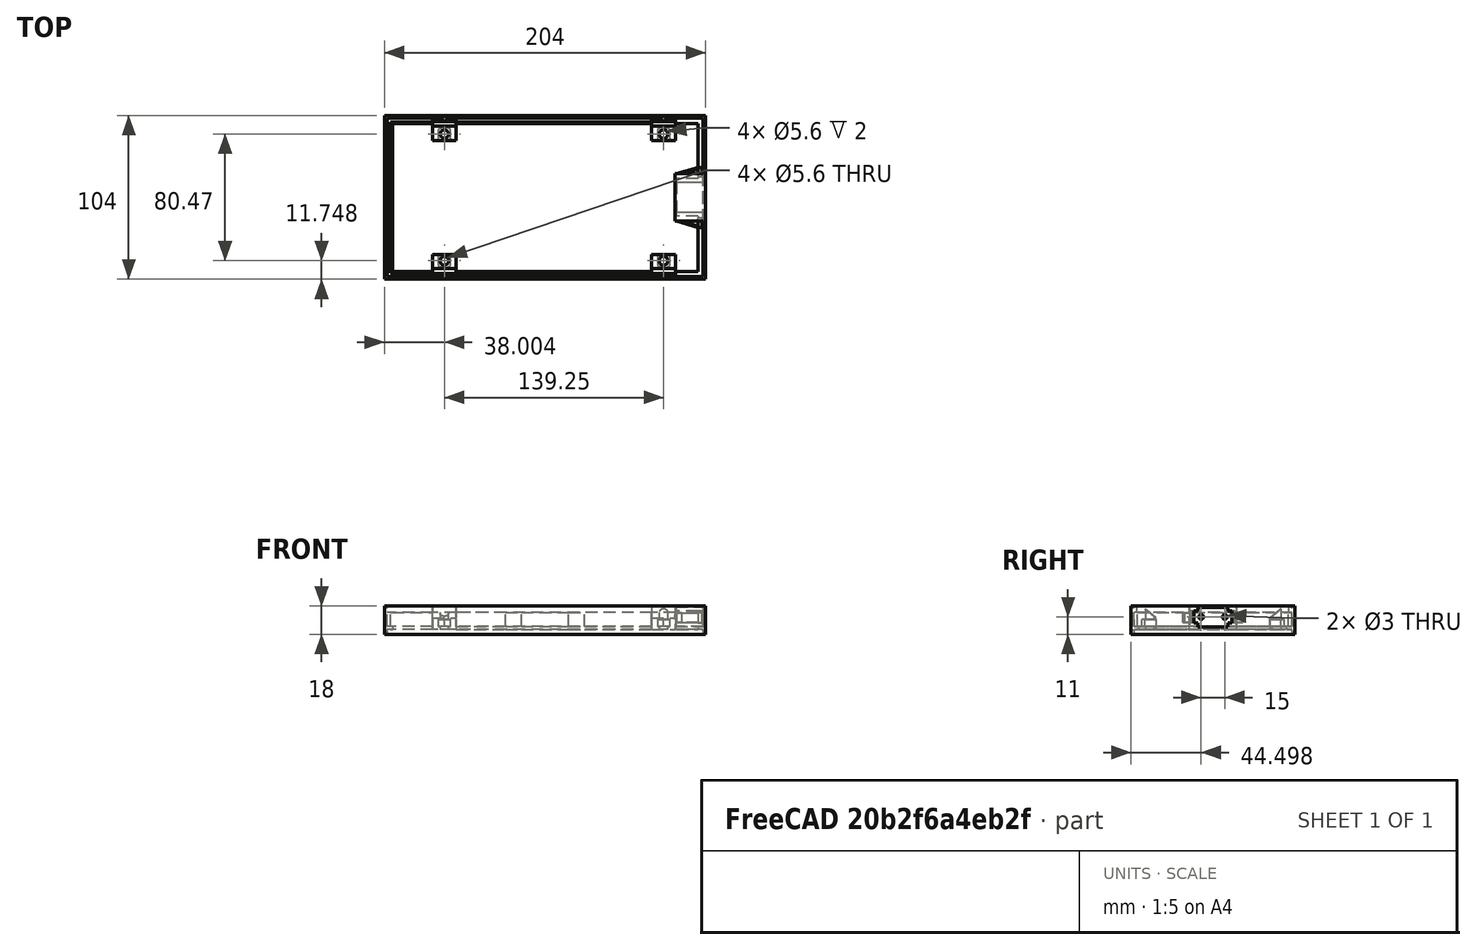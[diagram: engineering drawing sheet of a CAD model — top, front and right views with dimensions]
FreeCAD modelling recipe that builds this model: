
FCSTD DOCUMENT  (FreeCAD 0.18.3R)
Label: lamp.base.frame.230V.flat.shortside
License: All rights reserved
LicenseURL: http://en.wikipedia.org/wiki/All_rights_reserved
objects: Part::Extrusion×93, Part::Part2DObjectPython×50, Part::Cut×48, Part::Feature×38, Part::MultiFuse×21
note: 250 computed .brp shape members not serialized (recipe doc carries the construction recipe); baked Part::Feature solids carry a one-line shape summary decoded from their .brp

FEATURE [Part::Feature] Face035
  Placement = pos=(286.998,-351.852,-5.08221) rot=(0.57735,0.57735,0.57735;2.0944rad)
  shape: bbox 2e-07 x 3 x 7.5 mm, 1 faces, 0 solids (baked)
FEATURE [Part::Extrusion] Extrusion040
  Base = -> Face035
  Dir = (11.952,0,0)
  DirMode = 0
  FaceMakerClass = Part::FaceMakerBullseye
  LengthFwd = 0
  LengthRev = 0
  Solid = true
  Symmetric = false
FEATURE [Part::Part2DObjectPython] Rectangle114  # Draft 2D object (typed FeaturePython)
  ChamferSize = 0
  Columns = 1
  FilletRadius = 0
  Height = 14
  Length = 15
  MakeFace = true
  Placement = pos=(-44.4799,-326.495,6.4) rot=(0,0,1;0rad)
  Rows = 1
FEATURE [Part::Feature] Face048
  shape: bbox 4e-07 x 5 x 18 mm, 1 faces, 0 solids (baked)
FEATURE [Part::Part2DObjectPython] Circle027  # Draft 2D object (typed FeaturePython)
  FirstAngle = 0
  LastAngle = 0
  MakeFace = true
  Placement = pos=(-36.9799,-236.025,2.5e-14) rot=(1,0,0;3.14159rad)
  Radius = 2.8
FEATURE [Part::Part2DObjectPython] Rectangle106  # Draft 2D object (typed FeaturePython)
  ChamferSize = 0
  Columns = 1
  FilletRadius = 0
  Height = 14.0305
  Length = 15
  MakeFace = true
  Placement = pos=(-44.4799,-240.025,6) rot=(0,0,1;0rad)
  Rows = 1
FEATURE [Part::Part2DObjectPython] Circle058  # Draft 2D object (typed FeaturePython)
  FirstAngle = 0
  LastAngle = 0
  MakeFace = true
  Placement = pos=(141.399,-335.352,2) rot=(1,0,0;1.5708rad)
  Radius = 1.5
FEATURE [Part::Feature] Face037
  Placement = pos=(258.998,-351.852,-5.08221) rot=(0.57735,0.57735,0.57735;2.0944rad)
  shape: bbox 2e-07 x 3 x 7.5 mm, 1 faces, 0 solids (baked)
FEATURE [Part::Part2DObjectPython] Circle024  # Draft 2D object (typed FeaturePython)
  FirstAngle = 0
  LastAngle = 0
  MakeFace = true
  Placement = pos=(-176.23,-316.495,1.32e-13) rot=(1,0,0;3.14159rad)
  Radius = 2.8
FEATURE [Part::Part2DObjectPython] Wire005  # Draft 2D object (typed FeaturePython)
  ChamferSize = 0
  Closed = true
  End = (-172.23,-313.495,6)
  FilletRadius = 0
  Length = 29.8885
  MakeFace = true
  Placement = pos=(-176.23,-311.495,6) rot=(0,0,1;0rad)
  Points = (6) [(0,0,0),(-4,-2,-1.77636e-15),(-4,-8,0),(0,-10,0),(4,-8,8.88178e-16),(4,-2,1.77636e-15)]
  Start = (-176.23,-311.495,6)
  Subdivisions = 0
FEATURE [Part::Extrusion] Extrude150
  Base = -> Wire005
  Dir = (0,0,1)
  DirMode = 2
  FaceMakerClass = Part::FaceMakerBullseye
  LengthFwd = 4.4
  LengthRev = 0
  Placement = pos=(-2.8e-14,0,-4) rot=(0,0,1;0rad)
  Solid = false
  Symmetric = false
FEATURE [Part::Extrusion] Extrude151
  Base = -> Wire005
  Dir = (0,0,1)
  DirMode = 2
  FaceMakerClass = Part::FaceMakerBullseye
  LengthFwd = 4.4
  LengthRev = 0
  Placement = pos=(-2.8e-14,80.4695,-4) rot=(0,0,1;0rad)
  Solid = false
  Symmetric = false
FEATURE [Part::Extrusion] Extrude152
  Base = -> Wire005
  Dir = (0,0,1)
  DirMode = 2
  FaceMakerClass = Part::FaceMakerBullseye
  LengthFwd = 4.4
  LengthRev = 0
  Placement = pos=(139.25,0,-4) rot=(0,0,1;0rad)
  Solid = false
  Symmetric = false
FEATURE [Part::Extrusion] Extrude230
  Base = -> Circle058
  Dir = (0,-1,-2e-16)
  DirMode = 2
  FaceMakerClass = Part::FaceMakerBullseye
  LengthFwd = -2
  LengthRev = 0
  Solid = false
  Symmetric = false
FEATURE [Part::Extrusion] Extrude156
  Base = -> Rectangle106
  Dir = (0,0,1)
  DirMode = 2
  FaceMakerClass = Part::FaceMakerBullseye
  LengthFwd = -6.4
  LengthRev = 0
  Placement = pos=(0,0,0.4) rot=(0,0,1;0rad)
  Solid = false
  Symmetric = false
FEATURE [Part::Part2DObjectPython] Rectangle164  # Draft 2D object (typed FeaturePython)
  ChamferSize = 0
  Columns = 1
  FilletRadius = 0
  Height = 7
  Length = 2.5
  MakeFace = true
  Placement = pos=(131.899,-351.602,-1.5) rot=(0.57735,0.57735,0.57735;2.0944rad)
  Rows = 1
FEATURE [Part::Part2DObjectPython] Circle040  # Draft 2D object (typed FeaturePython)
  FirstAngle = 0
  LastAngle = 0
  MakeFace = true
  Placement = pos=(218.524,-261.633,-6) rot=(1,0,0;3.14159rad)
  Radius = 2.8
FEATURE [Part::Part2DObjectPython] Rectangle  # Draft 2D object (typed FeaturePython)
  ChamferSize = 0
  Columns = 1
  FilletRadius = 0
  Height = 14
  Length = 15
  MakeFace = true
  Placement = pos=(-183.73,-326.495,6) rot=(0,0,1;0rad)
  Rows = 1
FEATURE [Part::Extrusion] Extrude158
  Base = -> Rectangle
  Dir = (0,0,1)
  DirMode = 2
  FaceMakerClass = Part::FaceMakerBullseye
  LengthFwd = -6.4
  LengthRev = 0
  Placement = pos=(0,0,0.4) rot=(0,0,1;0rad)
  Solid = false
  Symmetric = false
FEATURE [Part::Part2DObjectPython] Rectangle162  # Draft 2D object (typed FeaturePython)
  ChamferSize = 0
  Columns = 1
  FilletRadius = 0
  Height = 0.2
  Length = 19
  MakeFace = true
  Placement = pos=(139.399,-353.852,-4.2) rot=(1,0,0;1.5708rad)
  Rows = 1
FEATURE [Part::Extrusion] Extrude231
  Base = -> Rectangle162
  Dir = (-3e-16,-1,2e-16)
  DirMode = 2
  FaceMakerClass = Part::FaceMakerBullseye
  LengthFwd = 10
  LengthRev = 0
  Placement = pos=(0,5,-9e-16) rot=(0,0,1;0rad)
  Solid = false
  Symmetric = false
FEATURE [Part::Feature] Face047
  Placement = pos=(-124.099,0,3.33221) rot=(0,0,1;0rad)
  shape: bbox 2 x 3e-07 x 7.5 mm, 1 faces, 0 solids (baked)
FEATURE [Part::Extrusion] Extrusion039
  Base = -> Rectangle
  Dir = (-28,0,0)
  DirMode = 0
  FaceMakerClass = Part::FaceMakerBullseye
  LengthFwd = 0
  LengthRev = 0
  Solid = true
  Symmetric = false
FEATURE [Part::Feature] Face038
  Placement = pos=(134.899,-349.102,5.25) rot=(0,0,1;3.14159rad)
  shape: bbox 5.5 x 2.5 x 2e-07 mm, 1 faces, 0 solids (baked)
FEATURE [Part::Extrusion] Extrusion044
  Base = -> Face038
  Dir = (0,1e-16,0.5)
  DirMode = 0
  FaceMakerClass = Part::FaceMakerBullseye
  LengthFwd = 0
  LengthRev = 0
  Solid = true
  Symmetric = false
FEATURE [Part::Feature] Face044
  Placement = pos=(-124.099,0,3.33221) rot=(0,0,1;0rad)
  shape: bbox 19 x 18.5 x 2e-07 mm, 1 faces, 0 solids (baked)
FEATURE [Part::Extrusion] Extrusion052
  Base = -> Face044
  Dir = (0,0,-0.2)
  DirMode = 0
  FaceMakerClass = Part::FaceMakerBullseye
  LengthFwd = 0
  LengthRev = 0
  Solid = true
  Symmetric = false
FEATURE [Part::Extrusion] Extrude155
  Base = -> Circle027
  Dir = (0,0,-1)
  DirMode = 2
  FaceMakerClass = Part::FaceMakerBullseye
  LengthFwd = -6.4
  LengthRev = 0
  Solid = false
  Symmetric = false
FEATURE [Part::Part2DObjectPython] Rectangle159  # Draft 2D object (typed FeaturePython)
  ChamferSize = 0
  Columns = 1
  FilletRadius = 0
  Height = 14.3
  Length = 1
  MakeFace = true
  Placement = pos=(166.939,-349.382,5.5) rot=(0,0,1;0.283123rad)
  Rows = 1
FEATURE [Part::Extrusion] Extrusion042
  Base = -> Face037
  Dir = (-14.0793,0,0)
  DirMode = 0
  FaceMakerClass = Part::FaceMakerBullseye
  LengthFwd = 0
  LengthRev = 0
  Solid = true
  Symmetric = false
FEATURE [Part::Extrusion] Extrusion059
  Base = -> Face048
  Dir = (50,1.5e-15,0)
  DirMode = 0
  FaceMakerClass = Part::FaceMakerBullseye
  LengthFwd = 0
  LengthRev = 0
  Solid = true
  Symmetric = false
FEATURE [Part::Part2DObjectPython] Rectangle073  # Draft 2D object (typed FeaturePython)
  ChamferSize = 0
  Columns = 1
  FilletRadius = 0
  Height = 100.5
  Length = 200.5
  MakeFace = true
  Placement = pos=(-212.48,-326.495,-1) rot=(0,0,1;0rad)
  Rows = 1
FEATURE [Part::Feature] Face050
  Placement = pos=(39.6248,-78.9998,4e-15) rot=(0,0,1;0rad)
  shape: bbox 1 x 3e-07 x 7.5 mm, 1 faces, 0 solids (baked)
FEATURE [Part::Feature] Face039
  Placement = pos=(0,0,-0.25) rot=(0,0,1;0rad)
  shape: bbox 2e-07 x 2.5 x 0.5 mm, 1 faces, 0 solids (baked)
FEATURE [Part::Extrusion] Extrusion045
  Base = -> Face039
  Dir = (2.49999,0,0)
  DirMode = 0
  FaceMakerClass = Part::FaceMakerBullseye
  LengthFwd = 0
  LengthRev = 0
  Solid = true
  Symmetric = false
FEATURE [Part::Part2DObjectPython] Rectangle111  # Draft 2D object (typed FeaturePython)
  ChamferSize = 0
  Columns = 1
  FilletRadius = 0
  Height = 4.4
  Length = 8
  MakeFace = true
  Placement = pos=(-32.9799,-313.495,2) rot=(0,0.707107,0.707107;3.14159rad)
  Rows = 1
FEATURE [Part::Extrusion] Extrude160
  Base = -> Rectangle111
  Dir = (0,1,-2e-16)
  DirMode = 2
  FaceMakerClass = Part::FaceMakerBullseye
  LengthFwd = 8
  LengthRev = 0
  Solid = false
  Symmetric = false
FEATURE [Part::Extrusion] Extrude237
  Base = -> Rectangle164
  Dir = (1,0,0)
  DirMode = 2
  FaceMakerClass = Part::FaceMakerBullseye
  LengthFwd = -2
  LengthRev = 0
  Solid = false
  Symmetric = false
FEATURE [Part::Part2DObjectPython] Rectangle113  # Draft 2D object (typed FeaturePython)
  ChamferSize = 0
  Columns = 1
  FilletRadius = 0
  Height = 14.0305
  Length = 15
  MakeFace = true
  Placement = pos=(-183.73,-240.025,6.4) rot=(0,0,1;0rad)
  Rows = 1
FEATURE [Part::Extrusion] Extrude
  Base = -> Circle024
  Dir = (0,0,-1)
  DirMode = 2
  FaceMakerClass = Part::FaceMakerBullseye
  LengthFwd = -6.4
  LengthRev = 0
  Solid = false
  Symmetric = false
FEATURE [Part::Part2DObjectPython] Rectangle074  # Draft 2D object (typed FeaturePython)
  ChamferSize = 0
  Columns = 1
  FilletRadius = 0
  Height = 96
  Length = 196
  MakeFace = true
  Placement = pos=(-210.23,-324.245,4.41e-14) rot=(0,0,1;0rad)
  Rows = 1
FEATURE [Part::Part2DObjectPython] Circle057  # Draft 2D object (typed FeaturePython)
  FirstAngle = 0
  LastAngle = 0
  MakeFace = true
  Placement = pos=(156.399,-335.352,2) rot=(1,0,0;1.5708rad)
  Radius = 1.5
FEATURE [Part::Extrusion] Extrude229
  Base = -> Circle057
  Dir = (0,-1,-2e-16)
  DirMode = 2
  FaceMakerClass = Part::FaceMakerBullseye
  LengthFwd = -2
  LengthRev = 0
  Solid = false
  Symmetric = false
FEATURE [Part::Extrusion] Extrude100
  Base = -> Rectangle073
  Dir = (0,2e-16,1)
  DirMode = 2
  FaceMakerClass = Part::FaceMakerBullseye
  LengthFwd = 2
  LengthRev = 0
  Placement = pos=(0,0,1) rot=(0,0,1;0rad)
  Solid = false
  Symmetric = false
FEATURE [Part::Part2DObjectPython] Rectangle109  # Draft 2D object (typed FeaturePython)
  ChamferSize = 0
  Columns = 1
  FilletRadius = 0
  Height = 4.4
  Length = 8
  MakeFace = true
  Placement = pos=(-172.23,-239.025,2) rot=(0,0.707107,0.707107;3.14159rad)
  Rows = 1
FEATURE [Part::Extrusion] Extrude162
  Base = -> Rectangle109
  Dir = (0,1,-2e-16)
  DirMode = 2
  FaceMakerClass = Part::FaceMakerBullseye
  LengthFwd = -8
  LengthRev = 0
  Solid = false
  Symmetric = false
FEATURE [Part::Extrusion] Extrude101
  Base = -> Rectangle074
  Dir = (0,2e-16,1)
  DirMode = 2
  FaceMakerClass = Part::FaceMakerBullseye
  LengthFwd = 10
  LengthRev = 0
  Solid = false
  Symmetric = false
FEATURE [Part::Part2DObjectPython] Rectangle107  # Draft 2D object (typed FeaturePython)
  ChamferSize = 0
  Columns = 1
  FilletRadius = 0
  Height = 14.0305
  Length = 15
  MakeFace = true
  Placement = pos=(-183.73,-240.025,6) rot=(0,0,1;0rad)
  Rows = 1
FEATURE [Part::Extrusion] Extrude157
  Base = -> Rectangle107
  Dir = (0,0,1)
  DirMode = 2
  FaceMakerClass = Part::FaceMakerBullseye
  LengthFwd = -6.4
  LengthRev = 0
  Placement = pos=(0,0,0.4) rot=(0,0,1;0rad)
  Solid = false
  Symmetric = false
FEATURE [Part::Cut] Cut054
  Base = -> Extrude157
  Tool = -> Extrude151
FEATURE [Part::Part2DObjectPython] Wire  # Draft 2D object (typed FeaturePython)
  ChamferSize = 0
  Closed = true
  End = (260.998,-353.852,-5.08221)
  FilletRadius = 0
  Length = 72
  MakeFace = true
  Placement = pos=(260.998,-353.852,2.41779) rot=(1,0,0;1.5708rad)
  Points = (12) [(0,0,0),(2.5,1.33227e-15,0),(2.5,2.25,0),(21.5,2.25,0),(21.5,8.88178e-16,0),(24,4.44089e-16,0),(24,-7.5,0),(21.5,-7.5,0),(21.5,-9.75,0),(2.5,-9.75,0),(2.5,-7.5,0),(0,-7.5,0)]
  Start = (260.998,-353.852,2.41779)
  Subdivisions = 0
FEATURE [Part::Part2DObjectPython] Rectangle110  # Draft 2D object (typed FeaturePython)
  ChamferSize = 0
  Columns = 1
  FilletRadius = 0
  Height = 4.4
  Length = 8
  MakeFace = true
  Placement = pos=(-172.23,-313.495,2) rot=(0,0.707107,0.707107;3.14159rad)
  Rows = 1
FEATURE [Part::Extrusion] Extrude161
  Base = -> Rectangle110
  Dir = (0,1,-2e-16)
  DirMode = 2
  FaceMakerClass = Part::FaceMakerBullseye
  LengthFwd = 8
  LengthRev = 0
  Solid = false
  Symmetric = false
FEATURE [Part::Part2DObjectPython] Rectangle071  # Draft 2D object (typed FeaturePython)
  ChamferSize = 0
  Columns = 1
  FilletRadius = 0
  Height = 100.5
  Length = 200.5
  MakeFace = true
  Placement = pos=(-212.48,-326.495,-1) rot=(0,0,1;0rad)
  Rows = 1
FEATURE [Part::Part2DObjectPython] Rectangle072  # Draft 2D object (typed FeaturePython)
  ChamferSize = 0
  Columns = 1
  FilletRadius = 0
  Height = 104
  Length = 204
  MakeFace = true
  Placement = pos=(-214.23,-328.245,-1) rot=(0,0,1;0rad)
  Rows = 1
  Support = -> [Rectangle071]
FEATURE [Part::Extrusion] Extrude099
  Base = -> Rectangle072
  Dir = (0,2e-16,1)
  DirMode = 2
  FaceMakerClass = Part::FaceMakerBullseye
  LengthFwd = 16
  LengthRev = 0
  Solid = false
  Symmetric = false
FEATURE [Part::Extrusion] Extrude098
  Base = -> Rectangle071
  Dir = (0,2e-16,1)
  DirMode = 2
  FaceMakerClass = Part::FaceMakerBullseye
  LengthFwd = 16
  LengthRev = 0
  Solid = false
  Symmetric = false
FEATURE [Part::Part2DObjectPython] Rectangle160  # Draft 2D object (typed FeaturePython)
  ChamferSize = 0
  Columns = 1
  FilletRadius = 0
  Height = 14.3
  Length = 0.88
  MakeFace = true
  Placement = pos=(129.899,-349.102,5.5) rot=(0,0,-1;0.283566rad)
  Rows = 1
FEATURE [Part::Part2DObjectPython] Rectangle117  # Draft 2D object (typed FeaturePython)
  ChamferSize = 0
  Columns = 1
  FilletRadius = 0
  Height = 2
  Length = 200.5
  MakeFace = true
  Placement = pos=(-212.48,-227.995,15) rot=(0,0,1;0rad)
  Rows = 1
FEATURE [Part::Part2DObjectPython] Wire008  # Draft 2D object (typed FeaturePython)
  ChamferSize = 0
  Closed = true
  End = (-183.73,-312.495,7.4)
  FilletRadius = 0
  Length = 28.3796
  MakeFace = true
  Placement = pos=(-183.73,-321.495,15) rot=(0,0,1;0rad)
  Points = (3) [(0,0,0),(0,9,0),(0,9,-7.6)]
  Start = (-183.73,-321.495,15)
  Subdivisions = 0
FEATURE [Part::Part2DObjectPython] Rectangle116  # Draft 2D object (typed FeaturePython)
  ChamferSize = 0
  Columns = 1
  FilletRadius = 0
  Height = 2
  Length = 200.5
  MakeFace = true
  Placement = pos=(-212.48,-326.495,15) rot=(0,0,1;0rad)
  Rows = 1
FEATURE [Part::Part2DObjectPython] Wire009  # Draft 2D object (typed FeaturePython)
  ChamferSize = 0
  Closed = true
  End = (-29.4799,-312.495,7.4)
  FilletRadius = 0
  Length = 28.3796
  MakeFace = true
  Placement = pos=(-29.4799,-321.495,15) rot=(0,0,1;0rad)
  Points = (3) [(0,0,0),(0,9,1.77636e-15),(0,9,-7.6)]
  Start = (-29.4799,-321.495,15)
  Subdivisions = 0
FEATURE [Part::Feature] Face040
  Placement = pos=(0,0,-0.25) rot=(0,0,1;0rad)
  shape: bbox 2e-07 x 2.5 x 6.5 mm, 1 faces, 0 solids (baked)
FEATURE [Part::Extrusion] Extrusion046
  Base = -> Face040
  Dir = (2.49999,0,0)
  DirMode = 0
  FaceMakerClass = Part::FaceMakerBullseye
  LengthFwd = 0
  LengthRev = 0
  Solid = true
  Symmetric = false
FEATURE [Part::Part2DObjectPython] Circle026  # Draft 2D object (typed FeaturePython)
  FirstAngle = 0
  LastAngle = 0
  MakeFace = true
  Placement = pos=(-36.9799,-316.495,2.5e-14) rot=(1,0,0;3.14159rad)
  Radius = 2.8
FEATURE [Part::Extrusion] Extrude154
  Base = -> Circle026
  Dir = (0,0,-1)
  DirMode = 2
  FaceMakerClass = Part::FaceMakerBullseye
  LengthFwd = -6.4
  LengthRev = 0
  Solid = false
  Symmetric = false
FEATURE [Part::Part2DObjectPython] Rectangle115  # Draft 2D object (typed FeaturePython)
  ChamferSize = 0
  Columns = 1
  FilletRadius = 0
  Height = 14
  Length = 15
  MakeFace = true
  Placement = pos=(-183.73,-326.495,6.4) rot=(0,0,1;0rad)
  Rows = 1
FEATURE [Part::Extrusion] Extrusion056
  Base = -> Rectangle159
  Dir = (1e-16,-2.1e-15,-7)
  DirMode = 0
  FaceMakerClass = Part::FaceMakerBullseye
  LengthFwd = 0
  LengthRev = 0
  Solid = true
  Symmetric = false
FEATURE [Part::Feature] Face008
  Placement = pos=(-44.4799,-240.025,7.4) rot=(0,0,1;0rad)
  shape: bbox 15 x 14.03 x 2e-07 mm, 1 faces, 0 solids (baked)
FEATURE [Part::Extrusion] Extrusion008
  Base = -> Face008
  Dir = (-2e-16,-2e-16,7.6)
  DirMode = 0
  FaceMakerClass = Part::FaceMakerBullseye
  LengthFwd = 0
  LengthRev = 0
  Solid = true
  Symmetric = false
FEATURE [Part::Part2DObjectPython] Wire006  # Draft 2D object (typed FeaturePython)
  ChamferSize = 0
  Closed = true
  End = (-29.4799,-240.025,7.4)
  FilletRadius = 0
  Length = 28.4334
  MakeFace = true
  Placement = pos=(-29.4799,-230.995,15) rot=(0.57735,0.57735,0.57735;2.0944rad)
  Points = (3) [(0,0,0),(-9.03045,0,0),(-9.03045,-7.6,0)]
  Start = (-29.4799,-230.995,15)
  Subdivisions = 0
  Support = -> [Extrusion008]
FEATURE [Part::Extrusion] Extrude148
  Base = -> Wire005
  Dir = (0,0,1)
  DirMode = 2
  FaceMakerClass = Part::FaceMakerBullseye
  LengthFwd = 4.4
  LengthRev = 0
  Placement = pos=(139.25,80.4695,-4) rot=(0,0,1;0rad)
  Solid = false
  Symmetric = false
FEATURE [Part::Extrusion] Extrusion061
  Base = -> Face050
  Dir = (0,-0.300003,0)
  DirMode = 0
  FaceMakerClass = Part::FaceMakerBullseye
  LengthFwd = 0
  LengthRev = 0
  Solid = true
  Symmetric = false
FEATURE [Part::Feature] Face002
  shape: bbox 196 x 3e-07 x 2 mm, 1 faces, 0 solids (baked)
FEATURE [Part::Extrusion] Extrusion003
  Base = -> Face002
  Dir = (0,1,-2e-16)
  DirMode = 0
  FaceMakerClass = Part::FaceMakerBullseye
  LengthFwd = 0
  LengthRev = 0
  Solid = true
  Symmetric = false
FEATURE [Part::Feature] Face001
  shape: bbox 3e-07 x 96 x 2 mm, 1 faces, 0 solids (baked)
FEATURE [Part::Extrusion] Extrusion002
  Base = -> Face001
  Dir = (1,0,0)
  DirMode = 0
  FaceMakerClass = Part::FaceMakerBullseye
  LengthFwd = 0
  LengthRev = 0
  Solid = true
  Symmetric = false
FEATURE [Part::Extrusion] Extrude168
  Base = -> Wire006
  Dir = (1,0,0)
  DirMode = 2
  FaceMakerClass = Part::FaceMakerBullseye
  LengthFwd = -180
  LengthRev = 0
  Solid = false
  Symmetric = false
FEATURE [Part::Part2DObjectPython] Wire007  # Draft 2D object (typed FeaturePython)
  ChamferSize = 0
  Closed = true
  End = (-183.73,-240.025,7.4)
  FilletRadius = 0
  Length = 28.4334
  MakeFace = true
  Placement = pos=(-183.73,-230.995,15) rot=(0,0,1;0rad)
  Points = (3) [(0,0,0),(0,-9.03045,0),(0,-9.03045,-7.6)]
  Start = (-183.73,-230.995,15)
  Subdivisions = 0
  Support = -> [Extrude168]
FEATURE [Part::Cut] Cut052
  Base = -> Extrude158
  Tool = -> Extrude150
FEATURE [Part::Cut] Cut053
  Base = -> Cut052
  Tool = -> Extrude
FEATURE [Part::Cut] Cut059
  Base = -> Cut053
  Tool = -> Extrude161
FEATURE [Part::Part2DObjectPython] Circle041  # Draft 2D object (typed FeaturePython)
  FirstAngle = 0
  LastAngle = 0
  MakeFace = true
  Placement = pos=(79.2741,-261.633,-6) rot=(1,0,0;3.14159rad)
  Radius = 2.8
FEATURE [Part::Extrusion] Extrude190
  Base = -> Circle040
  Dir = (0,0,-1)
  DirMode = 2
  FaceMakerClass = Part::FaceMakerBullseye
  LengthFwd = -40
  LengthRev = 0
  Solid = false
  Symmetric = false
FEATURE [Part::Part2DObjectPython] Circle025  # Draft 2D object (typed FeaturePython)
  FirstAngle = 0
  LastAngle = 0
  MakeFace = true
  Placement = pos=(-176.23,-236.025,2.3e-14) rot=(1,0,0;3.14159rad)
  Radius = 2.8
  Support = -> [Extrude]
FEATURE [Part::Extrusion] Extrude153
  Base = -> Circle025
  Dir = (0,0,-1)
  DirMode = 2
  FaceMakerClass = Part::FaceMakerBullseye
  LengthFwd = -6.4
  LengthRev = 0
  Solid = false
  Symmetric = false
FEATURE [Part::Cut] Cut055
  Base = -> Cut054
  Tool = -> Extrude153
FEATURE [Part::Part2DObjectPython] Circle042  # Draft 2D object (typed FeaturePython)
  FirstAngle = 0
  LastAngle = 0
  MakeFace = true
  Placement = pos=(79.2741,-342.102,-6) rot=(1,0,0;3.14159rad)
  Radius = 2.8
FEATURE [Part::Extrusion] Extrude192
  Base = -> Circle042
  Dir = (0,0,-1)
  DirMode = 2
  FaceMakerClass = Part::FaceMakerBullseye
  LengthFwd = -40
  LengthRev = 0
  Solid = false
  Symmetric = false
FEATURE [Part::Extrusion] Extrude191
  Base = -> Circle041
  Dir = (0,0,-1)
  DirMode = 2
  FaceMakerClass = Part::FaceMakerBullseye
  LengthFwd = -40
  LengthRev = 0
  Solid = false
  Symmetric = false
FEATURE [Part::Feature] Face007
  Placement = pos=(-183.73,-240.025,7.4) rot=(0,0,1;0rad)
  shape: bbox 15 x 14.03 x 2e-07 mm, 1 faces, 0 solids (baked)
FEATURE [Part::Extrusion] Extrusion007
  Base = -> Face007
  Dir = (-2e-16,-2e-16,7.6)
  DirMode = 0
  FaceMakerClass = Part::FaceMakerBullseye
  LengthFwd = 0
  LengthRev = 0
  Solid = true
  Symmetric = false
FEATURE [Part::Cut] Cut063
  Base = -> Extrusion007
  Tool = -> Extrude168
FEATURE [Part::Extrusion] Extrude169
  Base = -> Wire007
  Dir = (-15,0,0)
  DirLink = -> Extrusion007 [Edge4]
  DirMode = 1
  FaceMakerClass = Part::FaceMakerBullseye
  LengthFwd = -160
  LengthRev = 0
  Solid = false
  Symmetric = false
FEATURE [Part::Extrusion] Extrusion057
  Base = -> Rectangle160
  Dir = (0,-2.1e-15,-7)
  DirMode = 0
  FaceMakerClass = Part::FaceMakerBullseye
  LengthFwd = 0
  LengthRev = 0
  Solid = true
  Symmetric = false
FEATURE [Part::Extrusion] Extrusion038
  Base = -> Rectangle
  Dir = (-28,0,0)
  DirMode = 0
  FaceMakerClass = Part::FaceMakerBullseye
  LengthFwd = 0
  LengthRev = 0
  Solid = true
  Symmetric = false
FEATURE [Part::Cut] Cut060
  Base = -> Cut055
  Tool = -> Extrude162
FEATURE [Part::Cut] Cut056
  Base = -> Extrude156
  Tool = -> Extrude148
FEATURE [Part::Cut] Cut057
  Base = -> Cut056
  Tool = -> Extrude155
FEATURE [Part::Cut] Cut027
  Base = -> Extrude099
  Tool = -> Extrude098
FEATURE [Part::Extrusion] Extrude226
  Base = -> Wire
  Dir = (0,-1,2e-16)
  DirMode = 2
  FaceMakerClass = Part::FaceMakerBullseye
  LengthFwd = 10
  LengthRev = 0
  Placement = pos=(-124.099,8.56212,3.33221) rot=(0,0,1;0rad)
  Solid = false
  Symmetric = false
FEATURE [Part::Feature] Face005
  Placement = pos=(-183.73,-326.495,7.4) rot=(0,0,1;0rad)
  shape: bbox 15 x 14 x 2e-07 mm, 1 faces, 0 solids (baked)
FEATURE [Part::Extrusion] Extrusion
  Base = -> Face005
  Dir = (-2e-16,-2e-16,7.6)
  DirMode = 0
  FaceMakerClass = Part::FaceMakerBullseye
  LengthFwd = 0
  LengthRev = 0
  Solid = true
  Symmetric = false
FEATURE [Part::Extrusion] Extrude170
  Base = -> Wire008
  Dir = (15,0,0)
  DirLink = -> Extrusion [Edge10]
  DirMode = 1
  FaceMakerClass = Part::FaceMakerBullseye
  LengthFwd = 160
  LengthRev = 0
  Solid = false
  Symmetric = false
FEATURE [Part::Extrusion] Extrusion054
  Base = -> Face047
  Dir = (0,-0.400003,0)
  DirMode = 0
  FaceMakerClass = Part::FaceMakerBullseye
  LengthFwd = 0
  LengthRev = 0
  Solid = true
  Symmetric = false
FEATURE [Part::MultiFuse] Fusion081
  Shapes = -> [Extrusion042,Extrusion039,Extrusion040]
FEATURE [Part::Extrusion] Extrude164
  Base = -> Rectangle114
  Dir = (0,0,1)
  DirMode = 2
  FaceMakerClass = Part::FaceMakerBullseye
  LengthFwd = 1
  LengthRev = 0
  Solid = false
  Symmetric = false
FEATURE [Part::Cut] Cut028
  Base = -> Extrude100
  Tool = -> Extrude101
FEATURE [Part::Part2DObjectPython] Rectangle105  # Draft 2D object (typed FeaturePython)
  ChamferSize = 0
  Columns = 1
  FilletRadius = 0
  Height = 14
  Length = 15
  MakeFace = true
  Placement = pos=(-44.4799,-326.495,6) rot=(0,0,1;0rad)
  Rows = 1
FEATURE [Part::Extrusion] Extrude159
  Base = -> Rectangle105
  Dir = (0,0,1)
  DirMode = 2
  FaceMakerClass = Part::FaceMakerBullseye
  LengthFwd = -6.4
  LengthRev = 0
  Placement = pos=(0,0,0.4) rot=(0,0,1;0rad)
  Solid = false
  Symmetric = false
FEATURE [Part::Cut] Cut050
  Base = -> Extrude159
  Tool = -> Extrude152
FEATURE [Part::Cut] Cut051
  Base = -> Cut050
  Tool = -> Extrude154
FEATURE [Part::Cut] Cut058
  Base = -> Cut051
  Tool = -> Extrude160
FEATURE [Part::Extrusion] Extrude166
  Base = -> Rectangle113
  Dir = (0,0,1)
  DirMode = 2
  FaceMakerClass = Part::FaceMakerBullseye
  LengthFwd = 1
  LengthRev = 0
  Solid = false
  Symmetric = false
FEATURE [Part::MultiFuse] Fusion
  Shapes = -> [Cut060,Extrude166,Cut063]
FEATURE [Part::Feature] Face003
  shape: bbox 3e-07 x 96 x 2 mm, 1 faces, 0 solids (baked)
FEATURE [Part::Extrusion] Extrusion004
  Base = -> Face003
  Dir = (-1,0,0)
  DirMode = 0
  FaceMakerClass = Part::FaceMakerBullseye
  LengthFwd = 0
  LengthRev = 0
  Solid = true
  Symmetric = false
FEATURE [Part::Feature] Face004
  shape: bbox 196 x 3e-07 x 2 mm, 1 faces, 0 solids (baked)
FEATURE [Part::Extrusion] Extrusion005
  Base = -> Face004
  Dir = (0,-1,2e-16)
  DirMode = 0
  FaceMakerClass = Part::FaceMakerBullseye
  LengthFwd = 0
  LengthRev = 0
  Solid = true
  Symmetric = false
FEATURE [Part::MultiFuse] Fusion022
  Shapes = -> [Extrusion003,Extrusion004,Extrusion002,Extrusion005]
FEATURE [Part::Extrusion] Extrude173
  Base = -> Rectangle117
  Dir = (0,0,1)
  DirMode = 2
  FaceMakerClass = Part::FaceMakerBullseye
  LengthFwd = -4
  LengthRev = 0
  Solid = false
  Symmetric = false
FEATURE [Part::Cut] Cut062
  Base = -> Extrusion008
  Tool = -> Extrude169
FEATURE [Part::Feature] Face006
  Placement = pos=(-44.4799,-326.495,7.4) rot=(0,0,1;0rad)
  shape: bbox 15 x 14 x 2e-07 mm, 1 faces, 0 solids (baked)
FEATURE [Part::Extrusion] Extrusion006
  Base = -> Face006
  Dir = (-2e-16,-2e-16,7.6)
  DirMode = 0
  FaceMakerClass = Part::FaceMakerBullseye
  LengthFwd = 0
  LengthRev = 0
  Solid = true
  Symmetric = false
FEATURE [Part::Extrusion] Extrude171
  Base = -> Wire009
  Dir = (15,0,0)
  DirLink = -> Extrusion006 [Edge10]
  DirMode = 1
  FaceMakerClass = Part::FaceMakerBullseye
  LengthFwd = -160
  LengthRev = 0
  Solid = false
  Symmetric = false
FEATURE [Part::Cut] Cut065
  Base = -> Extrusion006
  Tool = -> Extrude170
FEATURE [Part::MultiFuse] Fusion034
  Shapes = -> [Cut058,Extrude164,Cut065]
FEATURE [Part::Extrusion] Extrude165
  Base = -> Rectangle115
  Dir = (0,0,1)
  DirMode = 2
  FaceMakerClass = Part::FaceMakerBullseye
  LengthFwd = 1
  LengthRev = 0
  Solid = false
  Symmetric = false
FEATURE [Part::Cut] Cut064
  Base = -> Extrusion
  Tool = -> Extrude171
FEATURE [Part::MultiFuse] Fusion033
  Shapes = -> [Cut059,Extrude165,Cut064]
FEATURE [Part::Feature] Face045
  Placement = pos=(-124.099,0,3.33221) rot=(0,0,1;0rad)
  shape: bbox 2 x 3e-07 x 7.5 mm, 1 faces, 0 solids (baked)
FEATURE [Part::Extrusion] Extrusion055
  Base = -> Face045
  Dir = (0,-0.400003,0)
  DirMode = 0
  FaceMakerClass = Part::FaceMakerBullseye
  LengthFwd = 0
  LengthRev = 0
  Solid = true
  Symmetric = false
FEATURE [Part::Feature] Face049
  Placement = pos=(39.6248,-78.9998,4e-15) rot=(0,0,1;0rad)
  shape: bbox 1 x 3e-07 x 7.5 mm, 1 faces, 0 solids (baked)
FEATURE [Part::Extrusion] Extrusion060
  Base = -> Face049
  Dir = (0,-0.300003,0)
  DirMode = 0
  FaceMakerClass = Part::FaceMakerBullseye
  LengthFwd = 0
  LengthRev = 0
  Solid = true
  Symmetric = false
FEATURE [Part::Feature] Face
  shape: bbox 204 x 104 x 2e-07 mm, 1 faces, 0 solids (baked)
FEATURE [Part::Extrusion] Extrusion001
  Base = -> Face
  Dir = (0,-5e-16,-2)
  DirMode = 0
  FaceMakerClass = Part::FaceMakerBullseye
  LengthFwd = 0
  LengthRev = 0
  Solid = true
  Symmetric = false
FEATURE [Part::MultiFuse] Fusion023
  Shapes = -> [Extrusion001,Cut027]
FEATURE [Part::MultiFuse] Fusion024
  Shapes = -> [Fusion023,Fusion022]
FEATURE [Part::Part2DObjectPython] Rectangle108  # Draft 2D object (typed FeaturePython)
  ChamferSize = 0
  Columns = 1
  FilletRadius = 0
  Height = 4.4
  Length = 8
  MakeFace = true
  Placement = pos=(-32.9799,-239.025,2) rot=(0,0.707107,0.707107;3.14159rad)
  Rows = 1
  Support = -> [Fusion024]
FEATURE [Part::Extrusion] Extrude163
  Base = -> Rectangle108
  Dir = (0,1,-2e-16)
  DirMode = 2
  FaceMakerClass = Part::FaceMakerBullseye
  LengthFwd = -8
  LengthRev = 0
  Solid = false
  Symmetric = false
FEATURE [Part::Cut] Cut061
  Base = -> Cut057
  Tool = -> Extrude163
FEATURE [Part::Part2DObjectPython] Rectangle112  # Draft 2D object (typed FeaturePython)
  ChamferSize = 0
  Columns = 1
  FilletRadius = 0
  Height = 14.0305
  Length = 15
  MakeFace = true
  Placement = pos=(-44.4799,-240.025,6.4) rot=(0,0,1;0rad)
  Rows = 1
  Support = -> [Cut061]
FEATURE [Part::Extrusion] Extrude167
  Base = -> Rectangle112
  Dir = (0,0,1)
  DirMode = 2
  FaceMakerClass = Part::FaceMakerBullseye
  LengthFwd = 1
  LengthRev = 0
  Solid = false
  Symmetric = false
FEATURE [Part::MultiFuse] Fusion032
  Shapes = -> [Cut061,Extrude167,Cut062]
FEATURE [Part::MultiFuse] Fusion035
  Shapes = -> [Fusion034,Fusion033,Fusion032,Fusion]
FEATURE [Part::Part2DObjectPython] Rectangle166  # Draft 2D object (typed FeaturePython)
  ChamferSize = 0
  Columns = 1
  FilletRadius = 0
  Height = 28
  Length = 3.4
  MakeFace = true
  Placement = pos=(162.899,-352.252,-1.75) rot=(0,0,1;1.5708rad)
  Rows = 1
FEATURE [Part::Extrusion] Extrusion058
  Base = -> Rectangle166
  Dir = (-1.39748e-07,1.39748e-07,7.5)
  DirMode = 0
  FaceMakerClass = Part::FaceMakerBullseye
  LengthFwd = 0
  LengthRev = 0
  Solid = true
  Symmetric = false
FEATURE [Part::Extrusion] Extrude172
  Base = -> Rectangle116
  Dir = (0,0,1)
  DirMode = 2
  FaceMakerClass = Part::FaceMakerBullseye
  LengthFwd = -4
  LengthRev = 0
  Solid = false
  Symmetric = false
FEATURE [Part::Cut] Cut066
  Base = -> Fusion035
  Tool = -> Extrude172
FEATURE [Part::Cut] Cut067
  Base = -> Cut066
  Tool = -> Extrude173
FEATURE [Part::MultiFuse] Fusion046
  Shapes = -> [Cut067,Fusion024]
FEATURE [Part::MultiFuse] Fusion047
  Placement = pos=(255.504,-25.6076,-6) rot=(0,0,1;0rad)
  Shapes = -> [Cut028,Fusion046]
FEATURE [Part::Part2DObjectPython] Circle039  # Draft 2D object (typed FeaturePython)
  FirstAngle = 0
  LastAngle = 0
  MakeFace = true
  Placement = pos=(218.524,-342.102,-6) rot=(1,0,0;3.14159rad)
  Radius = 2.8
  Support = -> [Fusion047]
FEATURE [Part::Extrusion] Extrude189
  Base = -> Circle039
  Dir = (0,0,-1)
  DirMode = 2
  FaceMakerClass = Part::FaceMakerBullseye
  LengthFwd = -40
  LengthRev = 0
  Solid = false
  Symmetric = false
FEATURE [Part::MultiFuse] Fusion065
  Shapes = -> [Extrude192,Extrude189,Extrude190,Extrude191]
FEATURE [Part::Cut] Cut077
  Base = -> Fusion047
  Tool = -> Fusion065
FEATURE [Part::Cut] Cut087
  Base = -> Cut077
  Tool = -> Extrude226
FEATURE [Part::Cut] Cut093
  Base = -> Cut087
  Tool = -> Extrude231
FEATURE [Part::Part2DObjectPython] Rectangle150  # Draft 2D object (typed FeaturePython)
  ChamferSize = 0
  Columns = 1
  FilletRadius = 0
  Height = 12
  Length = 19
  MakeFace = true
  Placement = pos=(263.498,-353.852,-7.33221) rot=(1,0,0;1.5708rad)
  Rows = 1
  Support = -> [Cut077]
FEATURE [Part::Extrusion] Extrude224
  Base = -> Rectangle150
  Dir = (0,-1,2e-16)
  DirMode = 2
  FaceMakerClass = Part::FaceMakerBullseye
  LengthFwd = -18.5
  LengthRev = 0
  Solid = false
  Symmetric = false
FEATURE [Part::Part2DObjectPython] Rectangle151  # Draft 2D object (typed FeaturePython)
  ChamferSize = 0
  Columns = 1
  FilletRadius = 0
  Height = 13
  Length = 30
  MakeFace = true
  Placement = pos=(257.998,-353.852,-7.33221) rot=(1,0,0;1.5708rad)
  Rows = 1
  Support = -> [Extrude224]
FEATURE [Part::Extrusion] Extrusion036
  Base = -> Rectangle151
  Dir = (-1e-16,18.5,-4.1e-15)
  DirMode = 0
  FaceMakerClass = Part::FaceMakerBullseye
  LengthFwd = 0
  LengthRev = 0
  Solid = true
  Symmetric = false
FEATURE [Part::Cut] Cut100
  Base = -> Cut093
  Tool = -> Extrusion058
FEATURE [Part::Part2DObjectPython] Rectangle167  # Draft 2D object (typed FeaturePython)
  ChamferSize = 0
  Columns = 1
  FilletRadius = 0
  Height = 16
  Length = 50
  MakeFace = true
  Placement = pos=(118.274,-361.852,9) rot=(0,0,1;0rad)
  Rows = 1
  Support = -> [Cut100]
FEATURE [Part::Cut] Cut083
  Base = -> Extrusion036
  Tool = -> Extrude224
FEATURE [Part::Part2DObjectPython] Rectangle153  # Draft 2D object (typed FeaturePython)
  ChamferSize = 0
  Columns = 1
  FilletRadius = 0
  Height = 7.5
  Length = 24
  MakeFace = true
  Placement = pos=(260.998,-353.852,-5.08221) rot=(1,0,0;1.5708rad)
  Rows = 1
  Support = -> [Cut083]
FEATURE [Part::Extrusion] Extrusion037
  Base = -> Rectangle153
  Dir = (5e-16,18.5,-4.1e-15)
  DirMode = 0
  FaceMakerClass = Part::FaceMakerBullseye
  LengthFwd = 0
  LengthRev = 0
  Solid = true
  Symmetric = false
FEATURE [Part::Part2DObjectPython] Rectangle152  # Draft 2D object (typed FeaturePython)
  ChamferSize = 0
  Columns = 1
  FilletRadius = 0
  Height = 30
  Length = 18.5
  MakeFace = true
  Placement = pos=(257.998,-353.852,-7.33221) rot=(0.707107,0.707107,0;3.14159rad)
  Rows = 1
  Support = -> [Cut083]
FEATURE [Part::Extrusion] Extrude225
  Base = -> Rectangle152
  Dir = (0,-2e-16,-1)
  DirMode = 2
  FaceMakerClass = Part::FaceMakerBullseye
  LengthFwd = 2
  LengthRev = 0
  Solid = false
  Symmetric = false
FEATURE [Part::Cut] Cut084
  Base = -> Cut083
  Tool = -> Extrusion037
FEATURE [Part::Cut] Cut085
  Base = -> Cut084
  Tool = -> Extrusion038
FEATURE [Part::MultiFuse] Fusion080
  Shapes = -> [Extrude225,Cut085]
FEATURE [Part::Cut] Cut086
  Base = -> Fusion080
  Placement = pos=(-124.099,0,3.33221) rot=(0,0,1;0rad)
  Tool = -> Fusion081
FEATURE [Part::Cut] Cut097
  Base = -> Cut086
  Tool = -> Extrusion052
FEATURE [Part::Cut] Cut098
  Base = -> Cut097
  Tool = -> Extrusion054
FEATURE [Part::Part2DObjectPython] Rectangle161  # Draft 2D object (typed FeaturePython)
  ChamferSize = 0
  Columns = 1
  FilletRadius = 0
  Height = 15
  Length = 30
  MakeFace = true
  Placement = pos=(133.899,-335.352,9) rot=(-1,0,0;1.5708rad)
  Rows = 1
  Support = -> [Cut086]
FEATURE [Part::Extrusion] Extrude228
  Base = -> Rectangle161
  Dir = (0,1,2e-16)
  DirMode = 2
  FaceMakerClass = Part::FaceMakerBullseye
  LengthFwd = 1
  LengthRev = 0
  Solid = false
  Symmetric = false
FEATURE [Part::Part2DObjectPython] Rectangle154  # Draft 2D object (typed FeaturePython)
  ChamferSize = 0
  Columns = 1
  FilletRadius = 0
  Height = 2.5
  Length = 5.5
  MakeFace = true
  Placement = pos=(136.899,-349.102,-1.75) rot=(0,0,1;3.14159rad)
  Rows = 1
  Support = -> [Cut086]
FEATURE [Part::Extrusion] Extrusion043
  Base = -> Rectangle154
  Dir = (-1e-16,1.7e-15,6.5)
  DirMode = 0
  FaceMakerClass = Part::FaceMakerBullseye
  LengthFwd = 0
  LengthRev = 0
  Placement = pos=(-1.99999,0,0.5) rot=(0,0,1;0rad)
  Solid = true
  Symmetric = false
FEATURE [Part::MultiFuse] Fusion082
  Placement = pos=(0,0,-0.25) rot=(0,0,1;0rad)
  Shapes = -> [Extrusion043,Extrusion044]
FEATURE [Part::Cut] Cut090
  Base = -> Extrude228
  Tool = -> Extrude229
FEATURE [Part::Cut] Cut096
  Base = -> Cut090
  Placement = pos=(-5.62499,0,0) rot=(0,0,1;0rad)
  Tool = -> Extrude230
FEATURE [Part::Cut] Cut088
  Base = -> Fusion082
  Tool = -> Extrusion045
FEATURE [Part::Cut] Cut089
  Base = -> Cut088
  Tool = -> Extrusion046
FEATURE [Part::Part2DObjectPython] Rectangle157  # Draft 2D object (typed FeaturePython)
  ChamferSize = 0
  Columns = 1
  FilletRadius = 0
  Height = 7
  Length = 2.5
  MakeFace = true
  Placement = pos=(162.899,-349.102,-1.5) rot=(0.57735,-0.57735,-0.57735;2.0944rad)
  Rows = 1
  Support = -> [Cut089]
FEATURE [Part::Extrusion] Extrude227
  Base = -> Rectangle157
  Dir = (-1,-2e-16,-2e-16)
  DirMode = 2
  FaceMakerClass = Part::FaceMakerBullseye
  LengthFwd = -3
  LengthRev = 0
  Solid = false
  Symmetric = false
FEATURE [Part::Part2DObjectPython] Rectangle163  # Draft 2D object (typed FeaturePython)
  ChamferSize = 0
  Columns = 1
  FilletRadius = 0
  Height = 7
  Length = 2.5
  MakeFace = true
  Placement = pos=(165.899,-351.602,-1.5) rot=(0.57735,0.57735,0.57735;2.0944rad)
  Rows = 1
  Support = -> [Extrude227]
FEATURE [Part::Extrusion] Extrude236
  Base = -> Rectangle163
  Dir = (1,0,0)
  DirMode = 2
  FaceMakerClass = Part::FaceMakerBullseye
  LengthFwd = 2
  LengthRev = 0
  Solid = false
  Symmetric = false
FEATURE [Part::Cut] Cut099
  Base = -> Cut098
  Tool = -> Extrusion055
FEATURE [Part::Extrusion] Extrude238
  Base = -> Rectangle167
  Dir = (0,0,1)
  DirMode = 2
  FaceMakerClass = Part::FaceMakerBullseye
  LengthFwd = -40
  LengthRev = 0
  Solid = false
  Symmetric = false
FEATURE [Part::Cut] Cut101
  Base = -> Cut100
  Tool = -> Extrude238
FEATURE [Part::MultiFuse] Fusion088
  Shapes = -> [Cut101,Extrusion059]
FEATURE [Part::MultiFuse] Fusion086
  Shapes = -> [Cut089,Extrude237,Extrusion057,Extrude227,Extrude236,Extrusion056]
FEATURE [Part::MultiFuse] Fusion087
  Placement = pos=(39.6248,-78.9998,4e-15) rot=(0,0,1;0rad)
  Shapes = -> [Fusion086,Cut099]
FEATURE [Part::Cut] Cut102
  Base = -> Fusion087
  Tool = -> Extrusion060
FEATURE [Part::Cut] Cut103
  Base = -> Cut102
  Placement = pos=(-45.2498,78.9998,9e-16) rot=(0,0,1;0rad)
  Tool = -> Extrusion061
FEATURE [Part::Part2DObjectPython] Rectangle168  # Draft 2D object (typed FeaturePython)
  ChamferSize = 0
  Columns = 1
  FilletRadius = 0
  Height = 30
  Length = 18.5
  MakeFace = true
  Placement = pos=(275.392,-497.324,9) rot=(0,0,1;1.5708rad)
  Rows = 1
  Support = -> [Cut103]
FEATURE [Part::Extrusion] Extrusion062
  Base = -> Rectangle168
  Dir = (2e-16,-3.1e-15,-15)
  DirMode = 0
  FaceMakerClass = Part::FaceMakerBullseye
  LengthFwd = 0
  LengthRev = 0
  Placement = pos=(-117.118,143.472,0) rot=(0,0,1;0rad)
  Solid = true
  Symmetric = false
FEATURE [Part::Cut] Cut104
  Base = -> Fusion088
  Tool = -> Extrusion062
FEATURE [Part::MultiFuse] Fusion076002
  Placement = pos=(-108.578,-445.126,9e-14) rot=(0,0,1;1.5708rad)
  Shapes = -> [Cut103,Cut096]
FEATURE [Part::Part2DObjectPython] Rectangle170  # Draft 2D object (typed FeaturePython)
  ChamferSize = 0
  Columns = 1
  FilletRadius = 0
  Height = 15
  Length = 30
  MakeFace = true
  Placement = pos=(245.274,-316.852,-6) rot=(0.57735,0.57735,0.57735;2.0944rad)
  Rows = 1
  Support = -> [Cut104]
FEATURE [Part::Extrusion] Extrude239
  Base = -> Rectangle170
  Dir = (1,-2e-16,-2e-16)
  DirMode = 2
  FaceMakerClass = Part::FaceMakerBullseye
  LengthFwd = -20
  LengthRev = 0
  Solid = false
  Symmetric = false
FEATURE [Part::Cut] Cut
  Base = -> Cut104
  Tool = -> Extrude239
FEATURE [Part::Feature] Face052
  shape: bbox 5e-07 x 5 x 15 mm, 1 faces, 0 solids (baked)
FEATURE [Part::Extrusion] Extrusion063
  Base = -> Face052
  Dir = (30,-6.6e-15,3e-16)
  DirMode = 0
  FaceMakerClass = Part::FaceMakerBullseye
  LengthFwd = 0
  LengthRev = 0
  Solid = true
  Symmetric = false
FEATURE [Part::MultiFuse] Fusion076003
  Shapes = -> [Extrusion063,Cut]
FEATURE [Part::MultiFuse] Fusion076004
  Shapes = -> [Fusion076002,Fusion076003]
FEATURE [Part::Feature] Face053
  Placement = pos=(-108.578,-450.751,9.6e-14) rot=(0,0,1;1.5708rad)
  shape: bbox 13.73 x 4 x 3e-07 mm, 1 faces, 0 solids (baked)
FEATURE [Part::Extrusion] Extrusion064
  Base = -> Face053
  Dir = (-2e-16,-2e-16,-1)
  DirMode = 0
  FaceMakerClass = Part::FaceMakerBullseye
  LengthFwd = 0
  LengthRev = 0
  Solid = true
  Symmetric = false
FEATURE [Part::Feature] Face054
  Placement = pos=(-108.578,-450.751,9.6e-14) rot=(0,0,1;1.5708rad)
  shape: bbox 2.5 x 2 x 2e-07 mm, 1 faces, 0 solids (baked)
FEATURE [Part::Extrusion] Extrusion065
  Base = -> Face054
  Dir = (-2e-16,-2e-16,-1)
  DirMode = 0
  FaceMakerClass = Part::FaceMakerBullseye
  LengthFwd = 0
  LengthRev = 0
  Solid = true
  Symmetric = false
FEATURE [Part::Feature] Face055
  Placement = pos=(-108.578,-450.751,9.6e-14) rot=(0,0,1;1.5708rad)
  shape: bbox 2.5 x 3 x 2e-07 mm, 1 faces, 0 solids (baked)
FEATURE [Part::Extrusion] Extrusion066
  Base = -> Face055
  Dir = (0,0,-1)
  DirMode = 0
  FaceMakerClass = Part::FaceMakerBullseye
  LengthFwd = 0
  LengthRev = 0
  Solid = true
  Symmetric = false
FEATURE [Part::Feature] Face056
  Placement = pos=(-108.578,-450.751,9.6e-14) rot=(0,0,1;1.5708rad)
  shape: bbox 13.73 x 4 x 3e-07 mm, 1 faces, 0 solids (baked)
FEATURE [Part::Extrusion] Extrusion067
  Base = -> Face056
  Dir = (-2e-16,-2e-16,-1)
  DirMode = 0
  FaceMakerClass = Part::FaceMakerBullseye
  LengthFwd = 0
  LengthRev = 0
  Solid = true
  Symmetric = false
FEATURE [Part::Feature] Face057
  Placement = pos=(-108.578,-450.751,9.6e-14) rot=(0,0,1;1.5708rad)
  shape: bbox 2.5 x 2 x 2e-07 mm, 1 faces, 0 solids (baked)
FEATURE [Part::Extrusion] Extrusion068
  Base = -> Face057
  Dir = (-2e-16,-2e-16,-1)
  DirMode = 0
  FaceMakerClass = Part::FaceMakerBullseye
  LengthFwd = 0
  LengthRev = 0
  Solid = true
  Symmetric = false
FEATURE [Part::Feature] Face058
  Placement = pos=(-108.578,-450.751,9.6e-14) rot=(0,0,1;1.5708rad)
  shape: bbox 2.5 x 3 x 2e-07 mm, 1 faces, 0 solids (baked)
FEATURE [Part::Extrusion] Extrusion069
  Base = -> Face058
  Dir = (-2e-16,-2e-16,-1)
  DirMode = 0
  FaceMakerClass = Part::FaceMakerBullseye
  LengthFwd = 0
  LengthRev = 0
  Solid = true
  Symmetric = false
FEATURE [Part::Cut] Cut105
  Base = -> Fusion076004
  Tool = -> Extrusion069
FEATURE [Part::Cut] Cut106
  Base = -> Cut105
  Tool = -> Extrusion068
FEATURE [Part::Cut] Cut107
  Base = -> Cut106
  Tool = -> Extrusion067
FEATURE [Part::Cut] Cut108
  Base = -> Cut107
  Tool = -> Extrusion066
FEATURE [Part::Cut] Cut109
  Base = -> Cut108
  Tool = -> Extrusion065
FEATURE [Part::Cut] Cut110
  Base = -> Cut109
  Tool = -> Extrusion064
FEATURE [Part::Feature] Face059
  shape: bbox 0.2794 x 1.041 x 2e-07 mm, 1 faces, 0 solids (baked)
FEATURE [Part::Extrusion] Extrusion070
  Base = -> Face059
  Dir = (-2e-16,-2e-16,-1)
  DirMode = 0
  FaceMakerClass = Part::FaceMakerBullseye
  LengthFwd = 0
  LengthRev = 0
  Solid = true
  Symmetric = false
FEATURE [Part::Feature] Face060
  shape: bbox 0.2462 x 0.9166 x 2e-07 mm, 1 faces, 0 solids (baked)
FEATURE [Part::Extrusion] Extrusion071
  Base = -> Face060
  Dir = (-2e-16,-2e-16,-1)
  DirMode = 0
  FaceMakerClass = Part::FaceMakerBullseye
  LengthFwd = 0
  LengthRev = 0
  Solid = true
  Symmetric = false
FEATURE [Part::Cut] Cut111
  Base = -> Cut110
  Tool = -> Extrusion071
FEATURE [Part::Cut] Cut112
  Base = -> Cut111
  Tool = -> Extrusion070
FEATURE [Part::Feature] Face061
  shape: bbox 2.5 x 2e-07 x 6 mm, 1 faces, 0 solids (baked)
FEATURE [Part::Extrusion] Extrusion072
  Base = -> Face061
  Dir = (-2e-16,-1,2e-16)
  DirMode = 0
  FaceMakerClass = Part::FaceMakerBullseye
  LengthFwd = 0
  LengthRev = 0
  Solid = true
  Symmetric = false
FEATURE [Part::Feature] Face062
  shape: bbox 2.5 x 2e-07 x 6 mm, 1 faces, 0 solids (baked)
FEATURE [Part::Extrusion] Extrusion073
  Base = -> Face062
  Dir = (2e-16,1,-2e-16)
  DirMode = 0
  FaceMakerClass = Part::FaceMakerBullseye
  LengthFwd = 0
  LengthRev = 0
  Solid = true
  Symmetric = false
FEATURE [Part::MultiFuse] Fusion076005
  Shapes = -> [Cut112,Extrusion072,Extrusion073]
FEATURE [Part::Feature] Face063
  Placement = pos=(255.504,-25.6076,-6) rot=(0,0,1;0rad)
  shape: bbox 124.3 x 2.25 x 4e-07 mm, 1 faces, 0 solids (baked)
FEATURE [Part::Extrusion] Extrusion074
  Base = -> Face063
  Dir = (0,0,9)
  DirMode = 0
  FaceMakerClass = Part::FaceMakerBullseye
  LengthFwd = 0
  LengthRev = 0
  Solid = true
  Symmetric = false
FEATURE [Part::Feature] Face064
  Placement = pos=(255.504,-25.6076,-6) rot=(0,0,1;0rad)
  shape: bbox 28.75 x 100.5 x 4.243e-07 mm, 1 faces, 0 solids (baked)
FEATURE [Part::Extrusion] Extrusion075
  Base = -> Face064
  Dir = (0,0,9)
  DirMode = 0
  FaceMakerClass = Part::FaceMakerBullseye
  LengthFwd = 0
  LengthRev = 0
  Solid = true
  Symmetric = false
FEATURE [Part::Feature] Face065
  shape: bbox 31.5 x 2.25 x 3e-07 mm, 1 faces, 0 solids (baked)
FEATURE [Part::Extrusion] Extrusion076
  Base = -> Face065
  Dir = (0,0,9)
  DirMode = 0
  FaceMakerClass = Part::FaceMakerBullseye
  LengthFwd = 0
  LengthRev = 0
  Solid = true
  Symmetric = false
FEATURE [Part::Feature] Face066
  shape: bbox 10 x 2.25 x 4e-07 mm, 1 faces, 0 solids (baked)
FEATURE [Part::Extrusion] Extrusion077
  Base = -> Face066
  Dir = (0,0,9)
  DirMode = 0
  FaceMakerClass = Part::FaceMakerBullseye
  LengthFwd = 0
  LengthRev = 0
  Solid = true
  Symmetric = false
FEATURE [Part::Feature] Face067
  shape: bbox 30 x 2.25 x 5e-07 mm, 1 faces, 0 solids (baked)
FEATURE [Part::Extrusion] Extrusion078
  Base = -> Face067
  Dir = (-1e-16,0,9)
  DirMode = 0
  FaceMakerClass = Part::FaceMakerBullseye
  LengthFwd = 0
  LengthRev = 0
  Solid = true
  Symmetric = false
FEATURE [Part::Feature] Face068
  shape: bbox 10 x 2.25 x 4e-07 mm, 1 faces, 0 solids (baked)
FEATURE [Part::Extrusion] Extrusion079
  Base = -> Face068
  Dir = (0,0,9)
  DirMode = 0
  FaceMakerClass = Part::FaceMakerBullseye
  LengthFwd = 0
  LengthRev = 0
  Solid = true
  Symmetric = false
FEATURE [Part::Feature] Face069
  shape: bbox 42.75 x 2.25 x 3e-07 mm, 1 faces, 0 solids (baked)
FEATURE [Part::Extrusion] Extrusion080
  Base = -> Face069
  Dir = (0,0,9)
  DirMode = 0
  FaceMakerClass = Part::FaceMakerBullseye
  LengthFwd = 0
  LengthRev = 0
  Solid = true
  Symmetric = false
